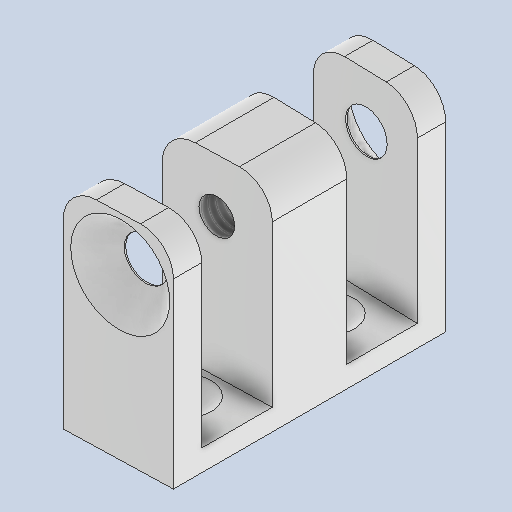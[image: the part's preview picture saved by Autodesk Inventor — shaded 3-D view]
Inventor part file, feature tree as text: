
AUTODESK INVENTOR PART (.ipt)
format: ipt  version: 2025 (Build 290162010, 162A)  size: 237,056 bytes
history: native  units: mm
features: sketch x7, hole x5, extrude x2, fillet x1, chamfer x1
ambient origin geometry x8: Origin, YZ Plane, XZ Plane, XY Plane, X Axis, Y Axis, Z Axis, Center Point
bodies: Volumenkörper1 (feature_tree)
feature tree (16):
  extrude  "Extrusion1"  Depth=3.0mm
  fillet  "Rundung1"  Radius=9.0mm
  sketch  "Skizze4"  dims[d37=13.333333mm d38=15.989748mm]
  extrude  "Extrusion3"  Depth=15.989748mm
  hole  "Bohrung4"  [1 undecoded]
  chamfer  "Fasen1"  Distance=2.0mm
  hole  "Bohrung5"  [1 undecoded]
  hole  "Bohrung6"  [1 undecoded]
  hole  "Bohrung7"  [1 undecoded]
  hole  "Bohrung8"  [1 undecoded]
  sketch  "Skizze1"  dims[d5=20.0mm d6=0.0mm d7=3.0mm d36=9.0mm]
  sketch  "Skizze6"  dims[d39=15.989748mm d40=10.0mm]
  sketch  "Skizze7"  dims[d41=6.6mm]
  sketch  "Skizze8"  dims[d42=6.6mm]
  sketch  "Skizze9"  dims[d43=13.840478mm d45=2.0mm d46=0.0mm]
  sketch  "Skizze10"  dims[d48=2.0mm d49=6.0mm d50=5.0mm d51=2.0mm d52=90.0deg d53=8.0mm d54=20.594885mm d55=1.5mm d56=2.0mm d57=45.0deg d58=26.0mm d59=13.333333mm d60=15.0mm d61=4.0mm d62=6.0mm d63=9.0mm d64=2.0mm d65=90.0deg d66=11.0mm d67=0.0mm d68=3.242mm d69=13.0mm d70=9.0mm d71=2.0mm d72=90.0deg d73=13.0mm d74=20.594885mm d75=15.0mm d76=4.0mm d77=12.0mm d78=9.0mm d79=2.0mm d80=90.0deg d81=13.0mm d82=0.0mm d83=3.242mm d84=13.0mm d85=9.0mm d86=2.0mm d87=90.0deg d88=13.0mm d89=20.594885mm]
note: 5 required parameter values undecoded (feature->parameter linkage not recoverable at this tier; creation-order binding heuristic only, values carry confidence <= 0.55)
